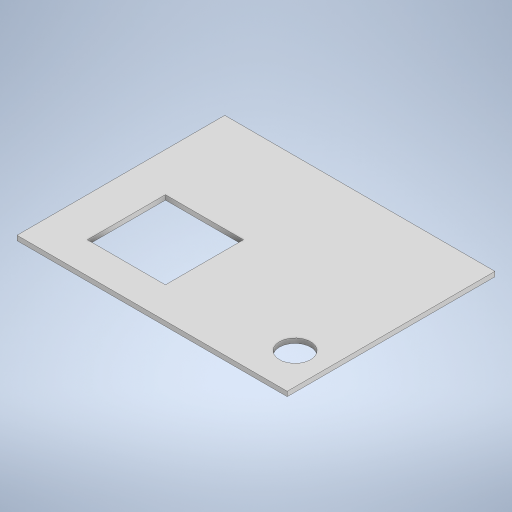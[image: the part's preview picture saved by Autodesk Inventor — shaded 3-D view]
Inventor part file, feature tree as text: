
AUTODESK INVENTOR PART (.ipt)
format: ipt  version: 2024.3 (Build 283343000, 343)  size: 235,520 bytes
history: native  units: mm
features: sketch x3, extrude x2, other x1, hole x1
ambient origin geometry x8: Origin, YZ Plane, XZ Plane, XY Plane, X Axis, Y Axis, Z Axis, Center Point
bodies: Body1 (feature_tree)
feature tree (7):
  other  "Těleso1"
  extrude  "Vysunutí1"  Depth=133.0mm
  extrude  "Vysunutí3"  Depth=173.0mm
  hole  "Díra1"  [1 undecoded]
  sketch  "Náčrt1"
  sketch  "Náčrt2"
  sketch  "Náčrt3"
note: 1 required parameter value undecoded (feature->parameter linkage not recoverable at this tier; creation-order binding heuristic only, values carry confidence <= 0.55)
